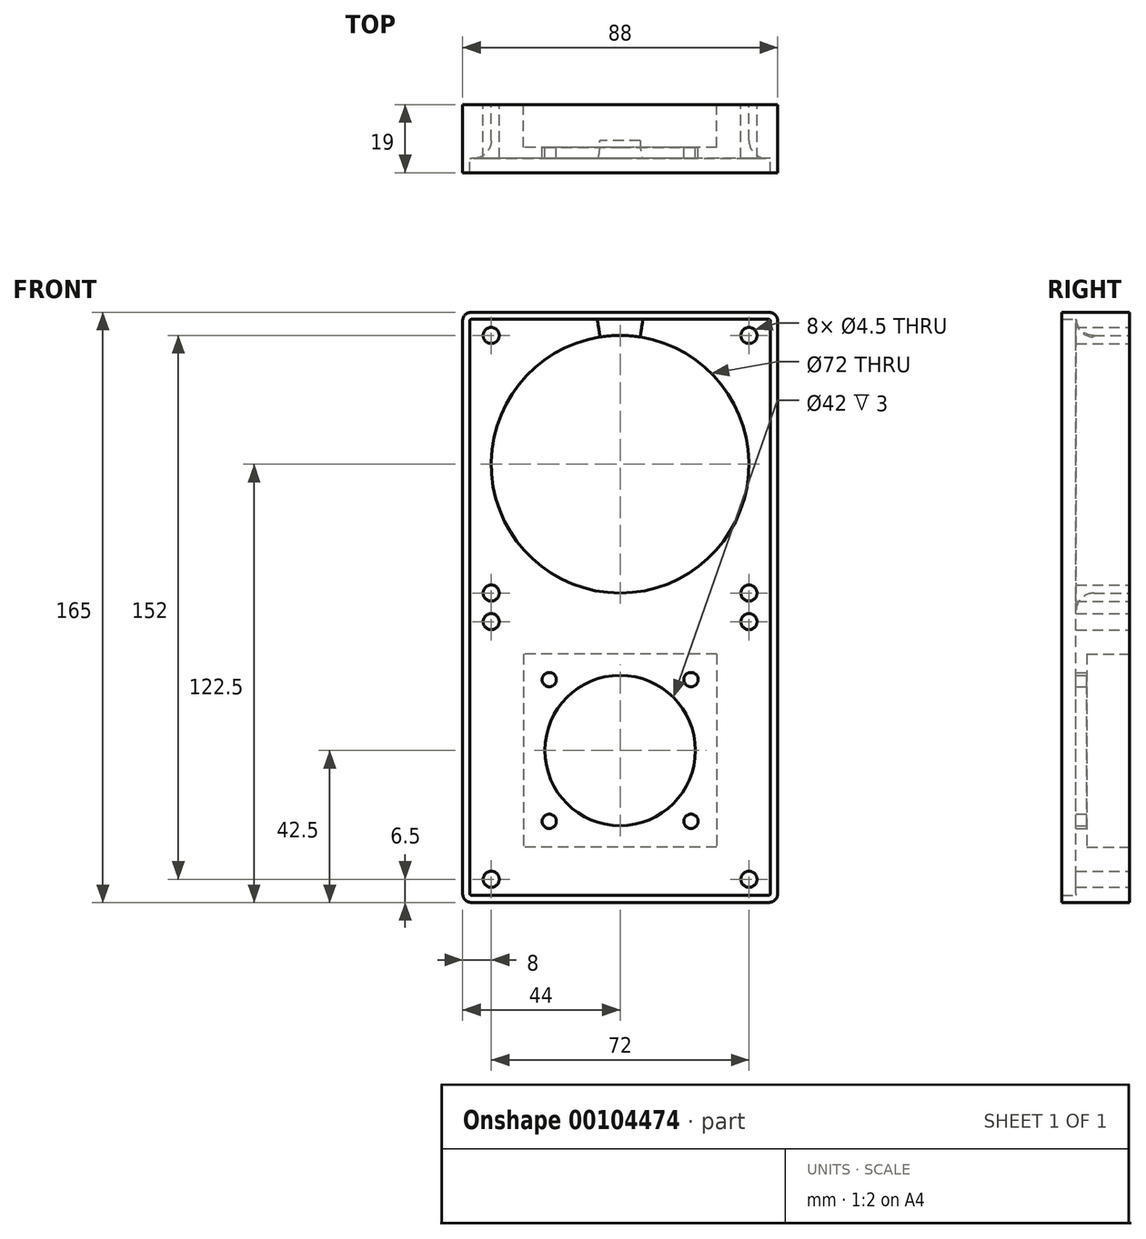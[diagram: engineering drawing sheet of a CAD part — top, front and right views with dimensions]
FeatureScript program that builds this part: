
annotation { "Feature Type Name" : "Feature", "Feature Type Description" : "" }
export const myFeature = defineFeature(function(context is Context, id is Id, definition is map)
    precondition{}
    {
        {
            var Q0;
            Q0=qCreatedBy(makeId("Front.planeOp"),FACE);
            var sketch = newSketch(context, id + "F0", { "sketchPlane" : qUnion([Q0])});
            skLineSegment(sketch, "E0.bottom", {"start": v(41.5, -82.5) * mm, "end": v(-41.5, -82.5) * mm});
            skLineSegment(sketch, "E0.top", {"start": v(41.5, 82.5) * mm, "end": v(-41.5, 82.5) * mm});
            skLineSegment(sketch, "E0.left", {"start": v(44, -80) * mm, "end": v(44, 80) * mm});
            skLineSegment(sketch, "E0.right", {"start": v(-44, -80) * mm, "end": v(-44, 80) * mm});
            skPoint(sketch, "E0.middle", {"position": v(0, 0) * mm});
            skLineSegment(sketch, "E1", {"start": v(0, 82.5) * mm, "end": v(0, -82.5) * mm, "construction": true});
            skLineSegment(sketch, "E2", {"start": v(-36, -82.5) * mm, "end": v(-36, 82.5) * mm, "construction": true});
            skLineSegment(sketch, "E3", {"start": v(36, 82.5) * mm, "end": v(36, -82.5) * mm, "construction": true});
            skLineSegment(sketch, "E4", {"start": v(-44, 0) * mm, "end": v(44, 0) * mm, "construction": true});
            skPoint(sketch, "E5", {"position": v(-36, -4) * mm});
            skLineSegment(sketch, "E6.bottom", {"start": v(-36, -4) * mm, "end": v(36, -4) * mm, "construction": true});
            skLineSegment(sketch, "E6.top", {"start": v(-36, -76) * mm, "end": v(36, -76) * mm, "construction": true});
            skLineSegment(sketch, "E6.left", {"start": v(-36, -4) * mm, "end": v(-36, -76) * mm, "construction": true});
            skLineSegment(sketch, "E6.right", {"start": v(36, -4) * mm, "end": v(36, -76) * mm, "construction": true});
            skLineSegment(sketch, "E7.MirrorCS", {"start": v(-36, 76) * mm, "end": v(36, 76) * mm, "construction": true});
            skLineSegment(sketch, "E8.MirrorCS", {"start": v(-36, 4) * mm, "end": v(-36, 76) * mm, "construction": true});
            skLineSegment(sketch, "E9.MirrorCS", {"start": v(36, 4) * mm, "end": v(36, 76) * mm, "construction": true});
            skLineSegment(sketch, "E10.MirrorCS", {"start": v(-36, 4) * mm, "end": v(36, 4) * mm, "construction": true});
            skCircle(sketch, "E11", {"center": v(-36, 76) * mm, "radius": 2.25 * mm});
            skCircle(sketch, "E12", {"center": v(36, 76) * mm, "radius": 2.25 * mm});
            skCircle(sketch, "E13", {"center": v(-36, 4) * mm, "radius": 2.25 * mm});
            skCircle(sketch, "E14", {"center": v(36, 4) * mm, "radius": 2.25 * mm});
            skCircle(sketch, "E15", {"center": v(36, -4) * mm, "radius": 2.25 * mm});
            skCircle(sketch, "E16", {"center": v(-36, -4) * mm, "radius": 2.25 * mm});
            skCircle(sketch, "E17", {"center": v(-36, -76) * mm, "radius": 2.25 * mm});
            skCircle(sketch, "E18", {"center": v(36, -76) * mm, "radius": 2.25 * mm});
            skPoint(sketch, "E19.visualSharp", {"position": v(-44, -82.5) * mm});
            skArc(sketch, "E19.filletArc", {"start": v(-44, -80) * mm, "mid": v(-43.27, -81.77) * mm, "end": v(-41.5, -82.5) * mm});
            skPoint(sketch, "E20.visualSharp", {"position": v(44, -82.5) * mm});
            skArc(sketch, "E20.filletArc", {"start": v(41.5, -82.5) * mm, "mid": v(43.27, -81.77) * mm, "end": v(44, -80) * mm});
            skPoint(sketch, "E21.visualSharp", {"position": v(44, 82.5) * mm});
            skArc(sketch, "E21.filletArc", {"start": v(44, 80) * mm, "mid": v(43.27, 81.77) * mm, "end": v(41.5, 82.5) * mm});
            skPoint(sketch, "E22.visualSharp", {"position": v(-44, 82.5) * mm});
            skArc(sketch, "E22.filletArc", {"start": v(-41.5, 82.5) * mm, "mid": v(-43.27, 81.77) * mm, "end": v(-44, 80) * mm});
            skLineSegment(sketch, "E23", {"start": v(-36, 76) * mm, "end": v(36, 4) * mm, "construction": true});
            skLineSegment(sketch, "E24", {"start": v(-36, -4) * mm, "end": v(36, -76) * mm, "construction": true});
            skPoint(sketch, "E25", {"position": v(-19.8, -20.2) * mm});
            skPoint(sketch, "E26", {"position": v(19.8, -59.8) * mm});
            skPoint(sketch, "E27", {"position": v(0, -40) * mm});
            skLineSegment(sketch, "E28.bottom", {"start": v(-19.8, -20.2) * mm, "end": v(19.8, -20.2) * mm, "construction": true});
            skLineSegment(sketch, "E28.top", {"start": v(-19.8, -59.8) * mm, "end": v(19.8, -59.8) * mm, "construction": true});
            skLineSegment(sketch, "E28.left", {"start": v(-19.8, -20.2) * mm, "end": v(-19.8, -59.8) * mm, "construction": true});
            skLineSegment(sketch, "E28.right", {"start": v(19.8, -20.2) * mm, "end": v(19.8, -59.8) * mm, "construction": true});
            skCircle(sketch, "E29", {"center": v(-19.8, -20.2) * mm, "radius": 2 * mm});
            skCircle(sketch, "E30", {"center": v(19.8, -20.2) * mm, "radius": 2 * mm});
            skCircle(sketch, "E31", {"center": v(19.8, -59.8) * mm, "radius": 2 * mm});
            skCircle(sketch, "E32", {"center": v(-19.8, -59.8) * mm, "radius": 2 * mm});
            skCircle(sketch, "E33", {"center": v(0, -40) * mm, "radius": 21 * mm});
            skCircle(sketch, "E34", {"center": v(0, 40) * mm, "radius": 36 * mm});
            skLineSegment(sketch, "E35.0", {"start": v(39, -77.5) * mm, "end": v(-39, -77.5) * mm});
            skLineSegment(sketch, "E35.1", {"start": v(39, -77.5) * mm, "end": v(39, 77.5) * mm});
            skLineSegment(sketch, "E35.2", {"start": v(39, 77.5) * mm, "end": v(-39, 77.5) * mm});
            skLineSegment(sketch, "E35.3", {"start": v(-39, -77.5) * mm, "end": v(-39, 77.5) * mm});
            skArc(sketch, "E36.0", {"start": v(-42, -80) * mm, "mid": v(-41.85, -80.35) * mm, "end": v(-41.5, -80.5) * mm});
            skLineSegment(sketch, "E36.1", {"start": v(41.5, -80.5) * mm, "end": v(-41.5, -80.5) * mm});
            skLineSegment(sketch, "E36.2", {"start": v(-42, -80) * mm, "end": v(-42, 80) * mm});
            skArc(sketch, "E36.3", {"start": v(41.5, -80.5) * mm, "mid": v(41.85, -80.35) * mm, "end": v(42, -80) * mm});
            skArc(sketch, "E36.4", {"start": v(-41.5, 80.5) * mm, "mid": v(-41.85, 80.35) * mm, "end": v(-42, 80) * mm});
            skLineSegment(sketch, "E36.5", {"start": v(41.5, 80.5) * mm, "end": v(-41.5, 80.5) * mm});
            skArc(sketch, "E36.6", {"start": v(42, 80) * mm, "mid": v(41.85, 80.35) * mm, "end": v(41.5, 80.5) * mm});
            skLineSegment(sketch, "E36.7", {"start": v(42, -80) * mm, "end": v(42, 80) * mm});
            skLineSegment(sketch, "E37.bottom", {"start": v(27, -13) * mm, "end": v(-27, -13) * mm});
            skLineSegment(sketch, "E37.top", {"start": v(27, -67) * mm, "end": v(-27, -67) * mm});
            skLineSegment(sketch, "E37.left", {"start": v(27, -13) * mm, "end": v(27, -67) * mm});
            skLineSegment(sketch, "E37.right", {"start": v(-27, -13) * mm, "end": v(-27, -67) * mm});
            skSolve(sketch);
        }
        {
            var Q0;
            Q0=makeQuery(id+"F0.imprint","IMPRINT",FACE,{"disambiguationData":[TD([[makeQuery(id+"F0.imprint","IMPRINT",EDGE,{"derivedFrom":sQuery(id+"F0.wireOp",EDGE,"E0.bottom")}),-1.0]])]});
            extrude(context, id + "F1", {"entities" : qUnion([Q0]), "depth" : 19 * mm});
        }
        {
            var Q0;
            {var subQ9=sQuery(id+"F0.wireOp",EDGE,"E35.1");Q0=makeQuery(id+"F0.imprint","IMPRINT",FACE,{"disambiguationData":[TD([[makeQuery(id+"F0.imprint","IMPRINT",EDGE,{"derivedFrom":subQ9}),-1.0]])]});}
            var Q1;
            Q1=makeQuery(id+"F0.imprint","IMPRINT",FACE,{"disambiguationData":[TD([[makeQuery(id+"F0.imprint","IMPRINT",EDGE,{"derivedFrom":sQuery(id+"F0.wireOp",EDGE,"E13")}),-1.0]])]});
            var Q2;
            Q2=makeQuery(id+"F0.imprint","IMPRINT",FACE,{"disambiguationData":[TD([[makeQuery(id+"F0.imprint","IMPRINT",EDGE,{"derivedFrom":sQuery(id+"F0.wireOp",EDGE,"E29")}),-1.0]])]});
            extrude(context, id + "F2", {"entities" : qUnion([Q0, Q1, Q2]), "operationType" : NewBodyOperationType.ADD, "depth" : 15 * mm});
        }
        {
            var Q0;
            Q0=makeQuery(id+"F0.imprint","IMPRINT",FACE,{"disambiguationData":[TD([[makeQuery(id+"F0.imprint","IMPRINT",EDGE,{"derivedFrom":sQuery(id+"F0.wireOp",EDGE,"E29")}),-1.0]])]});
            extrude(context, id + "F3", {"entities" : qUnion([Q0]), "operationType" : NewBodyOperationType.REMOVE, "depth" : 12 * mm});
        }
        {
            var Q0;
            Q0=makeQuery(id+"F2.opExtrude","CAP_EDGE",EDGE,{"disambiguationData":[OSD([sQuery(id+"F0.wireOp",EDGE,"E34")])],"isStart":false});
            fillet(context, id + "F4", {"entities" : qUnion([Q0]), "radius" : 5 * mm, "tangentPropagation" : true, "allowEdgeOverflow" : false});
        }
    });
